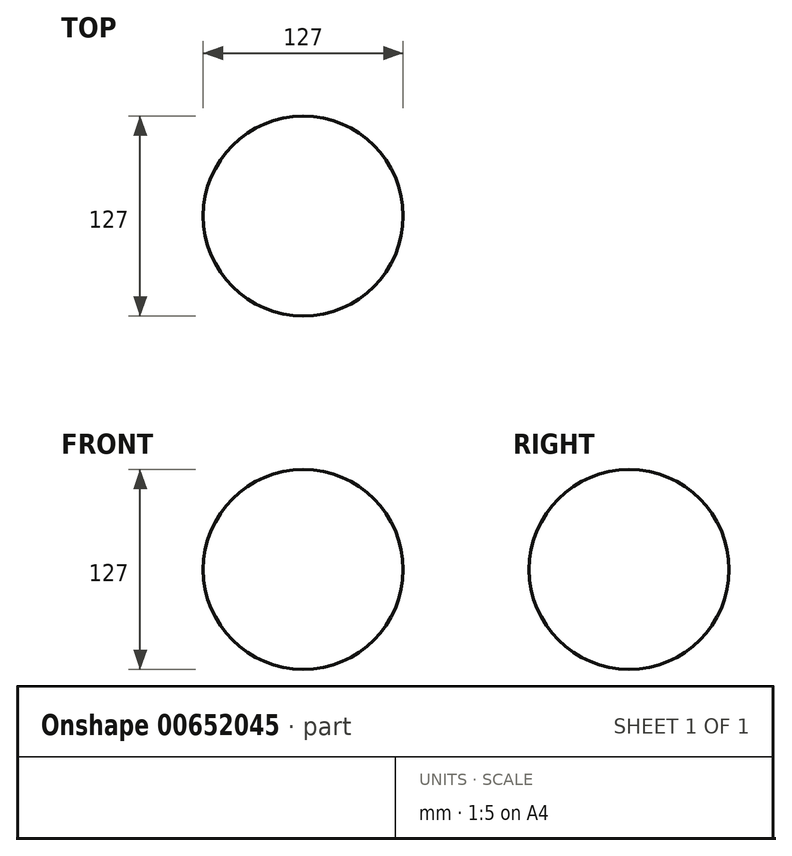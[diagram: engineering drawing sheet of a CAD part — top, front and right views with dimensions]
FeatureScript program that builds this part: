
annotation { "Feature Type Name" : "Feature", "Feature Type Description" : "" }
export const myFeature = defineFeature(function(context is Context, id is Id, definition is map)
    precondition{}
    {
        {
            var Q0;
            Q0=qCreatedBy(makeId("Front.planeOp"),FACE);
            var sketch = newSketch(context, id + "F0", { "sketchPlane" : qUnion([Q0])});
            skArc(sketch, "E0", {"start": v(0, 63.5) * mm, "mid": v(-63.5, 0) * mm, "end": v(0, -63.5) * mm});
            skLineSegment(sketch, "E1", {"start": v(0, 63.5) * mm, "end": v(0, -63.5) * mm});
            skSolve(sketch);
        }
        {
            var Q0;
            Q0=makeQuery(id+"F0.imprint","IMPRINT",FACE,{"disambiguationData":[TD([[makeQuery(id+"F0.imprint","IMPRINT",EDGE,{"derivedFrom":sQuery(id+"F0.wireOp",EDGE,"E0")}),1.0]])]});
            var Q1;
            Q1=sQuery(id+"F0.wireOp",EDGE,"E1");
            revolve(context, id + "F1", {"surfaceOperationType" : NewSurfaceOperationType.NEW, "entities" : qUnion([Q0]), "axis" : qUnion([Q1]), "revolveType" : RevolveType.SYMMETRIC, "angle" : 360 * degree});
        }
    });
